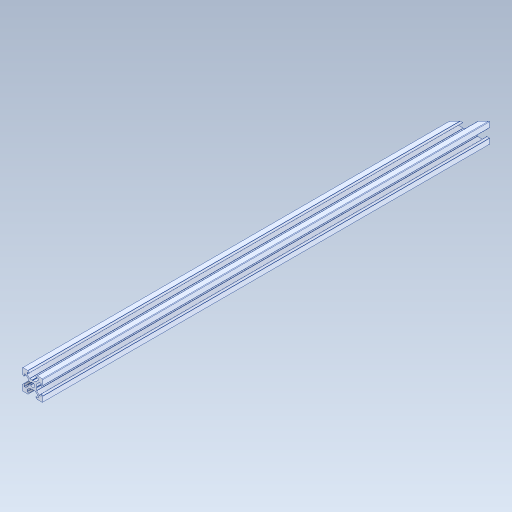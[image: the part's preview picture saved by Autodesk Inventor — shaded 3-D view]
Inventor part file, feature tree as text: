
AUTODESK INVENTOR PART (.ipt)
format: ipt  version: 2023 (Build 270158000, 158)  size: 343,552 bytes
history: mixed  units: in
note: dims shown in document units (in); Inventor stores cm internally (conversion verified against a paired STEP export)
features: other x3, extrude x1, sketch x1, imported_body x1
ambient origin geometry x8: Origin, YZ Plane, XZ Plane, XY Plane, X Axis, Y Axis, Z Axis, Center Point
bodies: Solid1 (imported_parasolid)
feature tree (6):
  other  "Annotations"
  other  "Boss-Extrude1"
  extrude  "Extrusion3"  TaperAngle=45.0deg  [1 undecoded]
  sketch  "Sketch4"  dims[d12=17.2047in d13=45.0deg d14=0.0in d15=0.0in d0=0.106in d1=0.114in d2=17.3228in]
  other  "Linear Dimension 1"
  imported_body  NMx_Import_Brep_tag  [imported B-rep: ~114 faces, bbox_mm=[20.0, 20.0, 437.0]]
note: 1 required parameter value undecoded (feature->parameter linkage not recoverable at this tier; creation-order binding heuristic only, values carry confidence <= 0.55)
